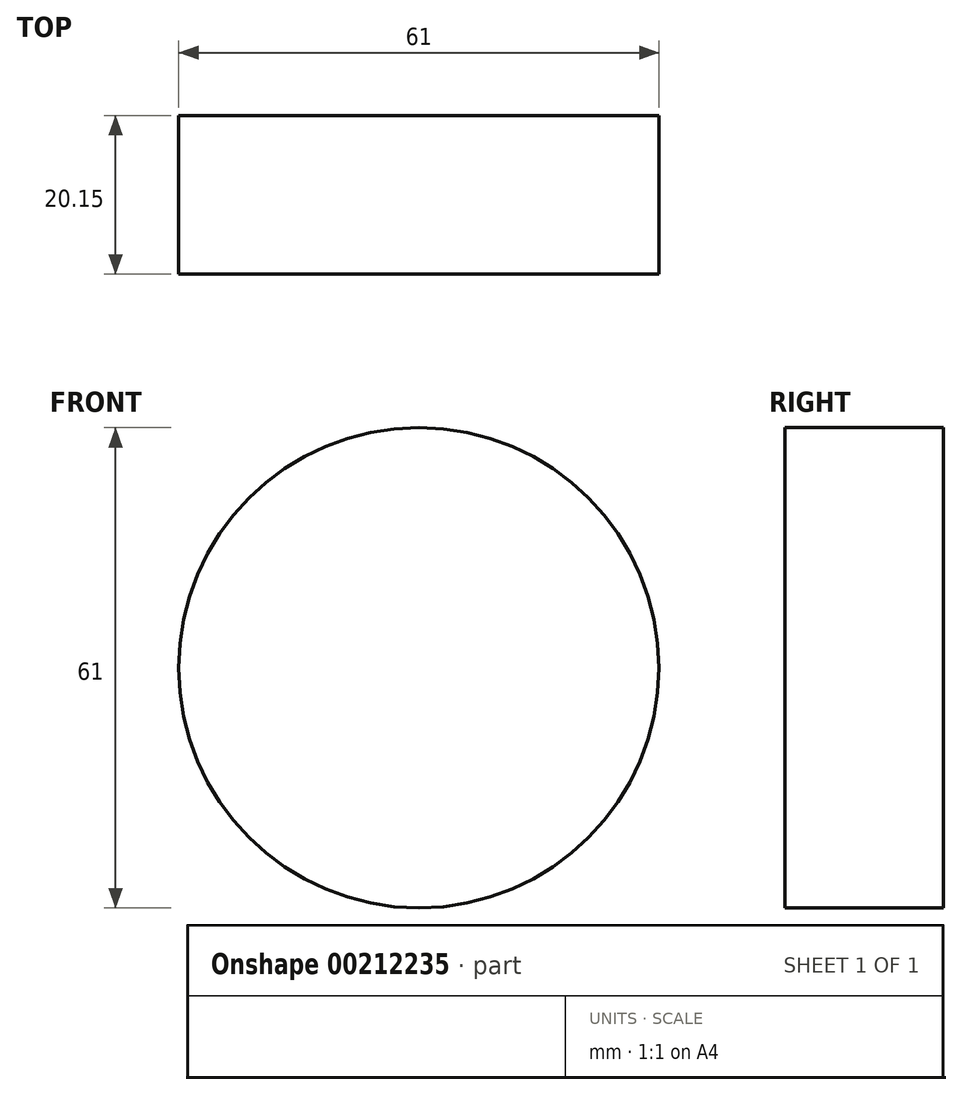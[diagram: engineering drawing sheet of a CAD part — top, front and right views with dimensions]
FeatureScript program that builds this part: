
annotation { "Feature Type Name" : "Feature", "Feature Type Description" : "" }
export const myFeature = defineFeature(function(context is Context, id is Id, definition is map)
    precondition{}
    {
        {
            var Q0;
            Q0=qCreatedBy(makeId("Front.planeOp"),FACE);
            var sketch = newSketch(context, id + "F0", { "sketchPlane" : qUnion([Q0])});
            skCircle(sketch, "E0", {"center": v(0, 0) * mm, "radius": 30.5 * mm});
            skSolve(sketch);
        }
        {
            var Q0;
            Q0 = qSketchRegion(id + "F0", true);
            extrude(context, id + "F1", {"entities" : qUnion([Q0]), "oppositeDirection" : true, "depth" : 20.15 * mm, "offsetDistance" : 25 * mm});
        }
    });
